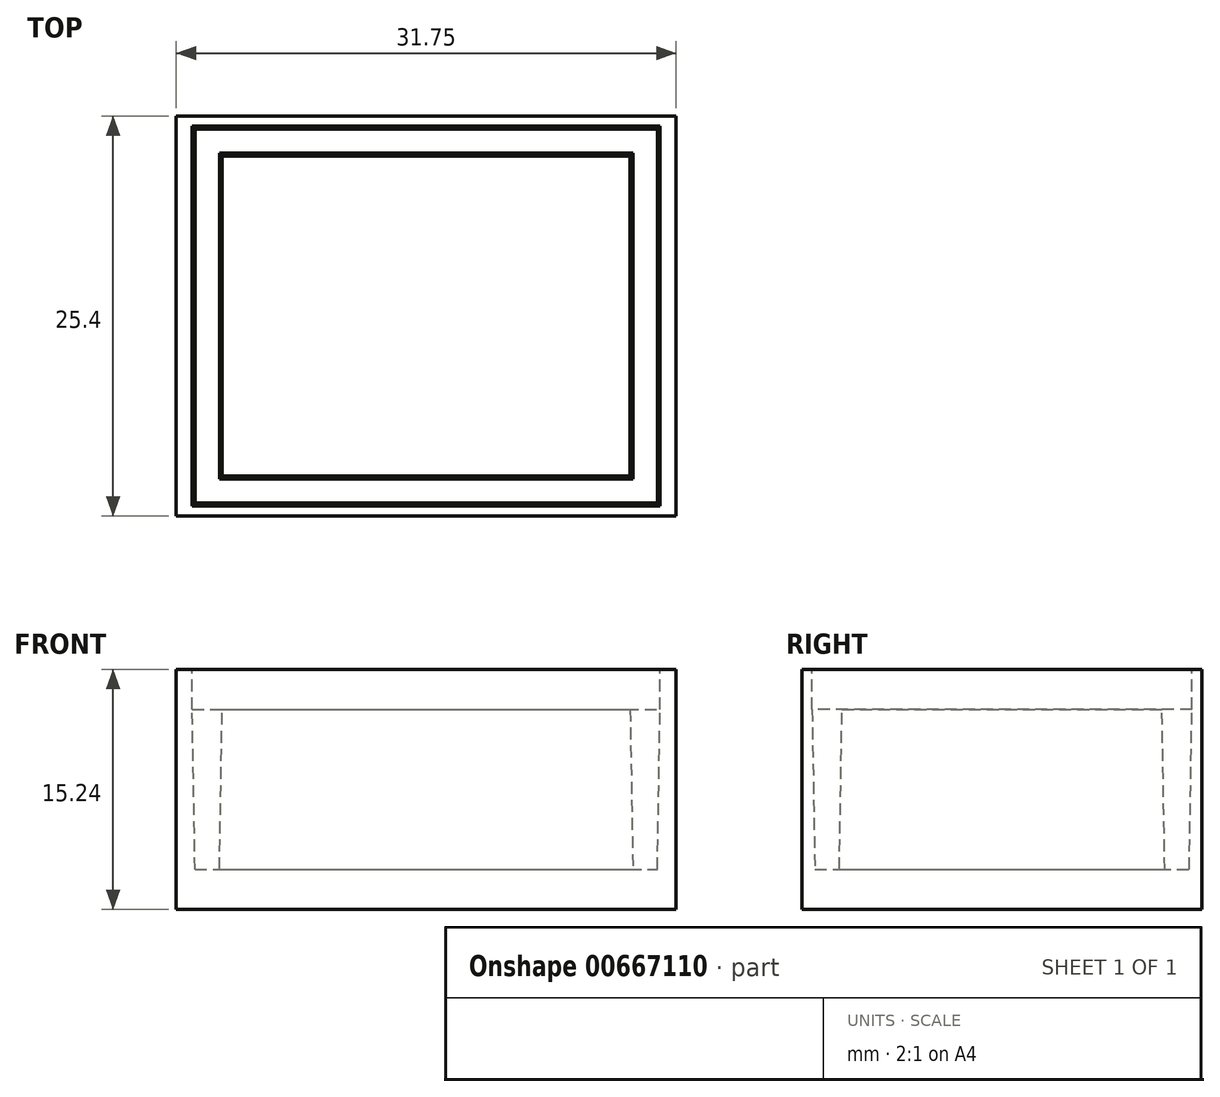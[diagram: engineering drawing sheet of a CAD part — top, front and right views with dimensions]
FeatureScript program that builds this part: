
annotation { "Feature Type Name" : "Feature", "Feature Type Description" : "" }
export const myFeature = defineFeature(function(context is Context, id is Id, definition is map)
    precondition{}
    {
        {
            var Q0;
            Q0=qCreatedBy(makeId("Top.planeOp"),FACE);
            var sketch = newSketch(context, id + "F0", { "sketchPlane" : qUnion([Q0])});
            skLineSegment(sketch, "E0.bottom", {"start": v(-31.75, 0) * mm, "end": v(0, 0) * mm});
            skLineSegment(sketch, "E0.top", {"start": v(-31.75, -25.4) * mm, "end": v(0, -25.4) * mm});
            skLineSegment(sketch, "E0.left", {"start": v(-31.75, 0) * mm, "end": v(-31.75, -25.4) * mm});
            skLineSegment(sketch, "E0.right", {"start": v(0, 0) * mm, "end": v(0, -25.4) * mm});
            skSolve(sketch);
        }
        {
            var Q0;
            Q0 = qSketchRegion(id + "F0", true);
            extrude(context, id + "F1", {"entities" : qUnion([Q0]), "depth" : 12.7 * mm, "offsetDistance" : 25.4 * mm});
        }
        {
            var Q0;
            Q0=makeQuery(id+"F1.opExtrude","CAP_FACE",FACE,{"disambiguationData":[OSD([sQuery(id+"F0.wireOp",EDGE,"E0.bottom"),sQuery(id+"F0.wireOp",EDGE,"E0.top"),sQuery(id+"F0.wireOp",EDGE,"E0.left"),sQuery(id+"F0.wireOp",EDGE,"E0.right")])],"isStart":false});
            var sketch = newSketch(context, id + "F2", { "sketchPlane" : qUnion([Q0])});
            skLineSegment(sketch, "E1", {"start": v(-15.88, 0) * mm, "end": v(-15.88, -25.4) * mm, "construction": true});
            skLineSegment(sketch, "E2", {"start": v(-31.75, -12.7) * mm, "end": v(0, -12.7) * mm, "construction": true});
            skLineSegment(sketch, "E3.bottom", {"start": v(-30.73, -0.63) * mm, "end": v(-1.02, -0.63) * mm});
            skLineSegment(sketch, "E3.top", {"start": v(-30.73, -24.77) * mm, "end": v(-1.02, -24.77) * mm});
            skLineSegment(sketch, "E3.left", {"start": v(-30.73, -0.64) * mm, "end": v(-30.73, -24.77) * mm});
            skLineSegment(sketch, "E3.right", {"start": v(-1.02, -0.64) * mm, "end": v(-1.02, -24.77) * mm});
            skLineSegment(sketch, "E4", {"start": v(-30.73, -12.7) * mm, "end": v(-1.02, -12.7) * mm, "construction": true});
            skLineSegment(sketch, "E5", {"start": v(-15.88, -0.63) * mm, "end": v(-15.88, -24.77) * mm, "construction": true});
            skSolve(sketch);
        }
        {
            var Q0;
            Q0 = qSketchRegion(id + "F2", true);
            extrude(context, id + "F3", {"entities" : qUnion([Q0]), "operationType" : NewBodyOperationType.REMOVE, "oppositeDirection" : true, "depth" : 2.54 * mm, "offsetDistance" : 25.4 * mm});
        }
        {
            var Q0;
            Q0=makeQuery(id+"F3.boolean.opBoolean","COPY",FACE,{"derivedFrom":makeQuery(id+"F3.opExtrude","CAP_FACE",FACE,{"disambiguationData":[OSD([sQuery(id+"F2.wireOp",EDGE,"E3.bottom"),sQuery(id+"F2.wireOp",EDGE,"E3.top"),sQuery(id+"F2.wireOp",EDGE,"E3.left"),sQuery(id+"F2.wireOp",EDGE,"E3.right")])],"isStart":false})});
            var sketch = newSketch(context, id + "F4", { "sketchPlane" : qUnion([Q0])});
            skLineSegment(sketch, "E6.bottom", {"start": v(-30.73, -0.63) * mm, "end": v(-1.02, -0.63) * mm});
            skLineSegment(sketch, "E6.top", {"start": v(-30.73, -24.77) * mm, "end": v(-1.02, -24.77) * mm});
            skLineSegment(sketch, "E6.left", {"start": v(-30.73, -0.63) * mm, "end": v(-30.73, -24.77) * mm});
            skLineSegment(sketch, "E6.right", {"start": v(-1.02, -0.63) * mm, "end": v(-1.02, -24.77) * mm});
            skLineSegment(sketch, "E7.bottom", {"start": v(-28.83, -2.54) * mm, "end": v(-2.92, -2.54) * mm});
            skLineSegment(sketch, "E7.top", {"start": v(-28.83, -22.86) * mm, "end": v(-2.92, -22.86) * mm});
            skLineSegment(sketch, "E7.left", {"start": v(-28.83, -2.54) * mm, "end": v(-28.83, -22.86) * mm});
            skLineSegment(sketch, "E7.right", {"start": v(-2.92, -2.54) * mm, "end": v(-2.92, -22.86) * mm});
            skSolve(sketch);
        }
        {
            var Q0;
            Q0 = qSketchRegion(id + "F4", true);
            extrude(context, id + "F5", {"entities" : qUnion([Q0]), "operationType" : NewBodyOperationType.REMOVE, "oppositeDirection" : true, "depth" : 10.16 * mm, "offsetDistance" : 25.4 * mm, "hasDraft" : true, "draftAngle" : 1 * degree, "draftPullDirection" : true});
        }
        {
            var Q0;
            {var subQ0=sQuery(id+"F0.wireOp",EDGE,"E0.bottom");var subQ1=sQuery(id+"F0.wireOp",EDGE,"E0.right");var subQ2=sQuery(id+"F0.wireOp",EDGE,"E0.top");var subQ3=sQuery(id+"F0.wireOp",EDGE,"E0.left");Q0=makeQuery(id+"F5.boolean.opBoolean","SPLIT",FACE,{"disambiguationData":[TD([makeQuery(id+"F1.opExtrude","SWEPT_FACE",FACE,{"disambiguationData":[OSD([subQ0])]})])],"derivedFrom":makeQuery(id+"F1.opExtrude","CAP_FACE",FACE,{"disambiguationData":[OSD([subQ0,subQ2,subQ3,subQ1])],"isStart":true})});}
            var sketch = newSketch(context, id + "F6", { "sketchPlane" : qUnion([Q0])});
            skLineSegment(sketch, "E8.bottom", {"start": v(0, 0) * mm, "end": v(-31.75, 0) * mm});
            skLineSegment(sketch, "E8.top", {"start": v(0, 25.4) * mm, "end": v(-31.75, 25.4) * mm});
            skLineSegment(sketch, "E8.left", {"start": v(0, 0) * mm, "end": v(0, 25.4) * mm});
            skLineSegment(sketch, "E8.right", {"start": v(-31.75, 0) * mm, "end": v(-31.75, 25.4) * mm});
            skSolve(sketch);
        }
        {
            var Q0;
            Q0 = qSketchRegion(id + "F6", true);
            extrude(context, id + "F7", {"entities" : qUnion([Q0]), "operationType" : NewBodyOperationType.ADD, "depth" : 2.54 * mm, "offsetDistance" : 25.4 * mm});
        }
    });
